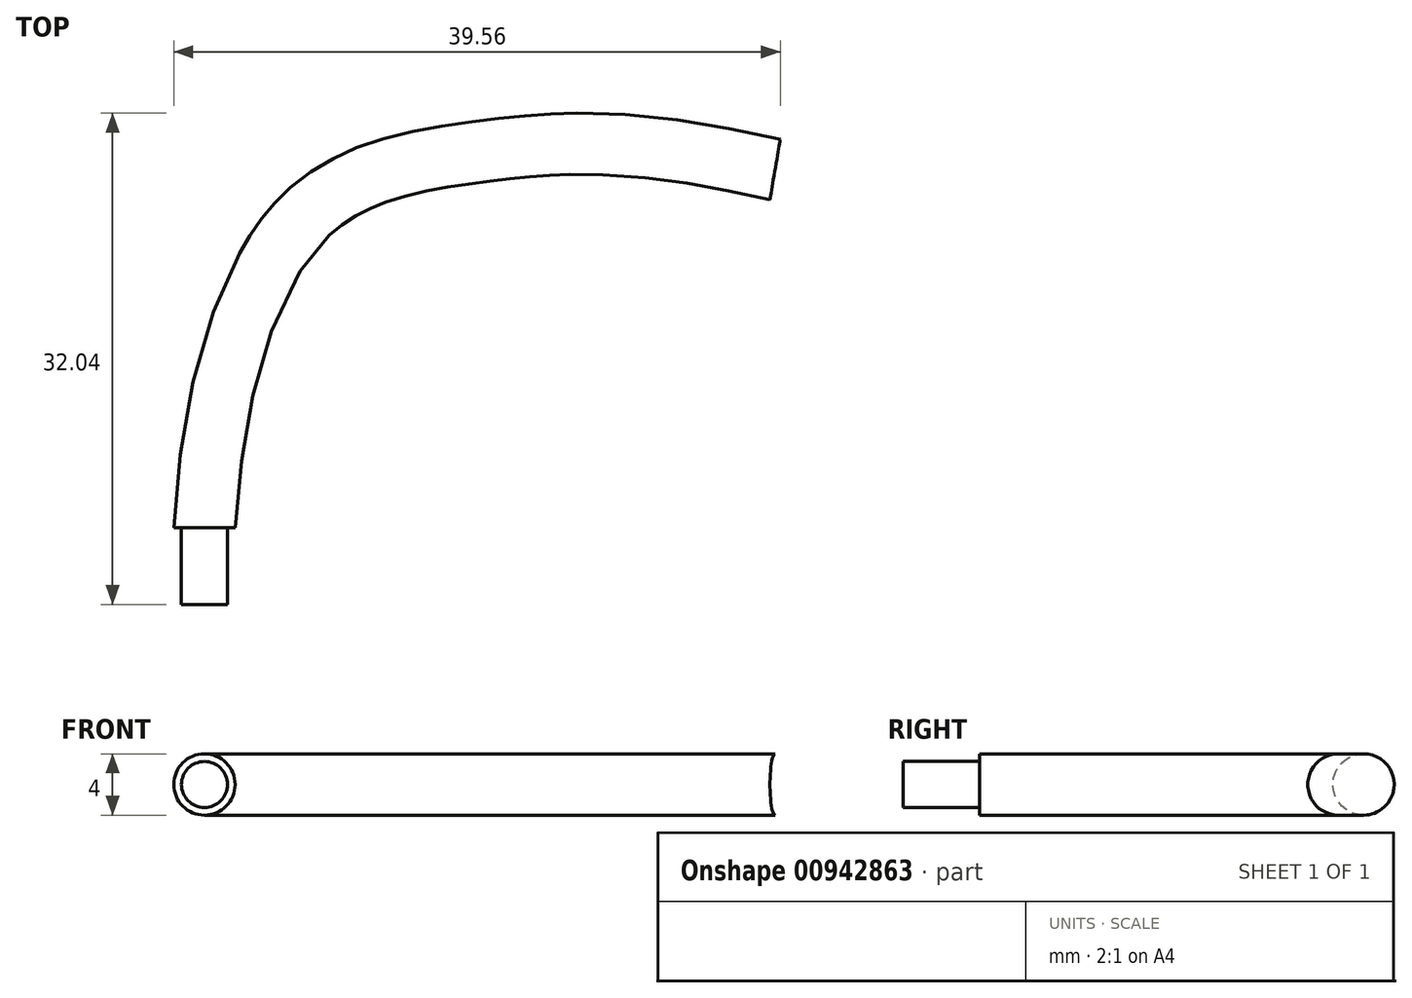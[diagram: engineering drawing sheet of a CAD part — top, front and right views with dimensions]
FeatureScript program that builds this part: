
annotation { "Feature Type Name" : "Feature", "Feature Type Description" : "" }
export const myFeature = defineFeature(function(context is Context, id is Id, definition is map)
    precondition{}
    {
        {
            var Q0;
            Q0=qCreatedBy(makeId("Front.planeOp"),FACE);
            var sketch = newSketch(context, id + "F0", { "sketchPlane" : qUnion([Q0])});
            skArc(sketch, "E0", {"start": v(-30.63, 1.9) * mm, "mid": v(-29.9, -2) * mm, "end": v(-29.58, 1.96) * mm});
            skArc(sketch, "E1", {"start": v(-29.58, 1.96) * mm, "mid": v(-30.1, 2) * mm, "end": v(-30.63, 1.9) * mm});
            skSolve(sketch);
        }
        {
            var Q0;
            Q0=qCreatedBy(makeId("Top.planeOp"),FACE);
            var sketch = newSketch(context, id + "F1", { "sketchPlane" : qUnion([Q0])});
            skFitSpline(sketch, "E2", {"points": [v(-30, 0) * mm, v(-23.58, 20.21) * mm, v(-12.06, 24.53) * mm, v(7.22, 23.38) * mm], "startDerivative": vector(3.63, 64.62) * mm, "endDerivative": vector(81.73, -18.73) * mm});
            skSolve(sketch);
        }
        {
            var Q0;
            Q0=makeQuery(id+"F0.imprint","IMPRINT",FACE,{"disambiguationData":[TD([[makeQuery(id+"F0.imprint","IMPRINT",EDGE,{"derivedFrom":sQuery(id+"F0.wireOp",EDGE,"E0")}),1.0]])]});
            var Q1;
            Q1=sQuery(id+"F0.wireOp",EDGE,"E0");
            var Q2;
            Q2=sQuery(id+"F1.wireOp",EDGE,"E2");
            sweep(context, id + "F2", {"profiles" : qUnion([Q0]), "surfaceProfiles" : qUnion([Q1]), "path" : qUnion([Q2])});
        }
        {
            var Q0;
            Q0=makeQuery(id+"F0.imprint","IMPRINT",FACE,{"disambiguationData":[TD([[makeQuery(id+"F0.imprint","IMPRINT",EDGE,{"derivedFrom":sQuery(id+"F0.wireOp",EDGE,"E0")}),1.0]])]});
            var sketch = newSketch(context, id + "F3", { "sketchPlane" : qUnion([Q0])});
            skCircle(sketch, "E3", {"center": v(-30, 0) * mm, "radius": 1.5 * mm});
            skSolve(sketch);
        }
        {
            var Q0;
            Q0=qSketchRegion(id+"F3",true);
            extrude(context, id + "F4", {"entities" : qUnion([Q0]), "depth" : 5 * mm});
        }
    });
